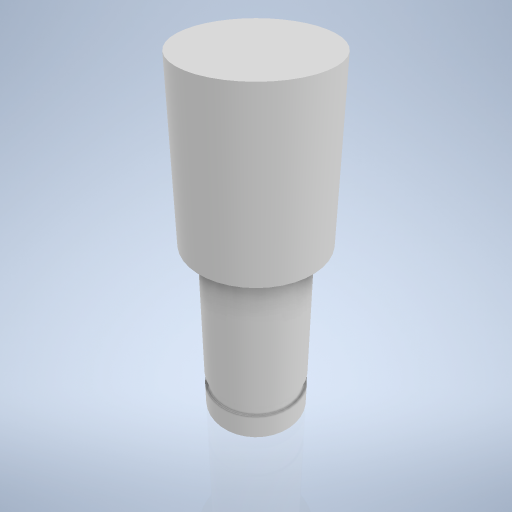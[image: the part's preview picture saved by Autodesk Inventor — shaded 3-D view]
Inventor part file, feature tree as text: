
AUTODESK INVENTOR PART (.ipt)
format: ipt  version: 2024.2 (Build 282272000, 272)  size: 248,320 bytes
history: native  units: mm
features: revolve x1, chamfer x1, sketch x1
ambient origin geometry x8: Origin, YZ Plane, XZ Plane, XY Plane, X Axis, Y Axis, Z Axis, Center Point
bodies: Volumenkörper1 (feature_tree)
feature tree (3):
  revolve  "Umdrehung1"
  chamfer  "Fasen1"  Distance=22.0mm
  sketch  "Skizze1"  dims[d0=10.0mm d1=22.0mm d3=9.0mm d4=0.8mm d5=8.0mm d6=6.0mm d7=5.7mm d8=90.0deg d9=0.5mm d10=2.0mm d11=45.0deg]
